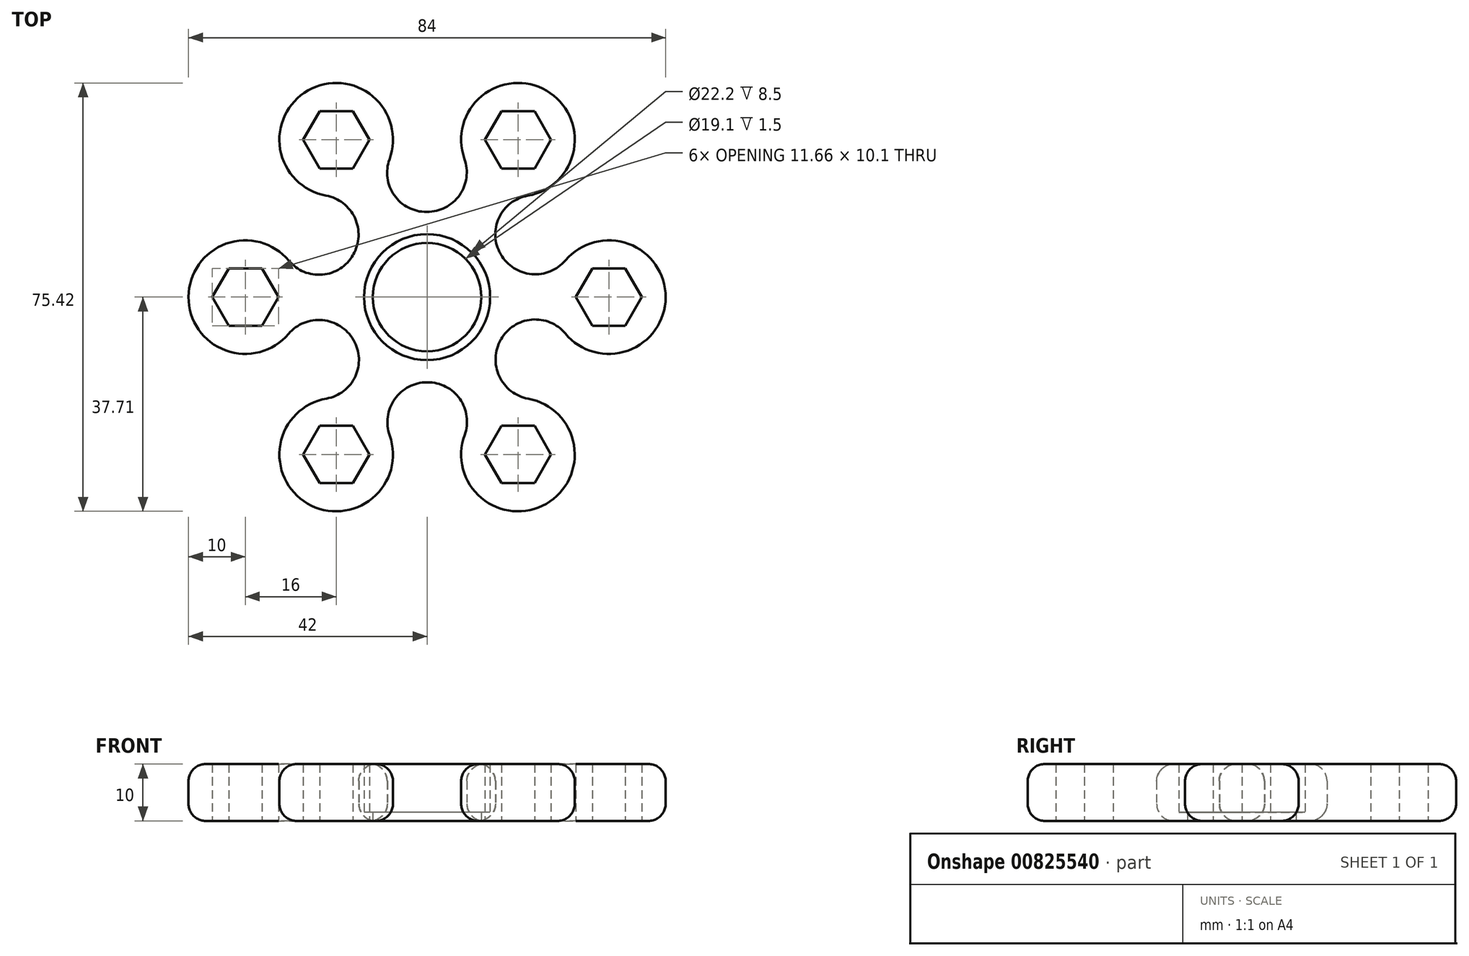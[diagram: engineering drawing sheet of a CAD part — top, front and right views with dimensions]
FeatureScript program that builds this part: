
annotation { "Feature Type Name" : "Feature", "Feature Type Description" : "" }
export const myFeature = defineFeature(function(context is Context, id is Id, definition is map)
    precondition{}
    {
        {
            var Q0;
            Q0=qCreatedBy(makeId("Top.planeOp"),FACE);
            var sketch = newSketch(context, id + "F0", { "sketchPlane" : qUnion([Q0])});
            skCircle(sketch, "E0", {"center": v(0, 0) * mm, "radius": 11.1 * mm});
            skLineSegment(sketch, "E1", {"start": v(0, 0) * mm, "end": v(32, 0) * mm});
            skCircle(sketch, "E2.cCircle", {"center": v(32, 0) * mm, "radius": 5.05 * mm, "construction": true});
            skLineSegment(sketch, "E2.0", {"start": v(34.92, -5.05) * mm, "end": v(29.08, -5.05) * mm});
            skLineSegment(sketch, "E2.1", {"start": v(29.08, -5.05) * mm, "end": v(26.17, 0) * mm});
            skLineSegment(sketch, "E2.2", {"start": v(26.17, 0) * mm, "end": v(29.08, 5.05) * mm});
            skLineSegment(sketch, "E2.3", {"start": v(29.08, 5.05) * mm, "end": v(34.92, 5.05) * mm});
            skLineSegment(sketch, "E2.4", {"start": v(34.92, 5.05) * mm, "end": v(37.83, 0) * mm});
            skLineSegment(sketch, "E2.5", {"start": v(37.83, 0) * mm, "end": v(34.92, -5.05) * mm});
            skPoint(sketch, "E2.0.midPoint", {"position": v(32, -5.05) * mm});
            skArc(sketch, "E3", {"start": v(12.99, 7.5) * mm, "mid": v(12.97, 7.54) * mm, "end": v(12.95, 7.58) * mm});
            skArc(sketch, "E4", {"start": v(24.33, -6.41) * mm, "mid": v(42, -0.04) * mm, "end": v(24.38, 6.48) * mm});
            skArc(sketch, "E5", {"start": v(12.99, 7.5) * mm, "mid": v(18.42, 4.04) * mm, "end": v(24.38, 6.48) * mm});
            skArc(sketch, "E6", {"start": v(24.33, -6.41) * mm, "mid": v(18.42, -3.96) * mm, "end": v(13.04, -7.42) * mm});
            skCircle(sketch, "E7.1.0", {"center": v(16, 27.71) * mm, "radius": 5.05 * mm, "construction": true});
            skArc(sketch, "E7.1.1", {"start": v(17.72, 17.86) * mm, "mid": v(21.04, 36.35) * mm, "end": v(6.58, 24.35) * mm});
            skPoint(sketch, "E7.1.2", {"position": v(20.37, 25.19) * mm});
            skLineSegment(sketch, "E7.1.3", {"start": v(13.08, 22.66) * mm, "end": v(10.17, 27.71) * mm});
            skArc(sketch, "E7.1.4", {"start": v(17.72, 17.86) * mm, "mid": v(12.64, 13.97) * mm, "end": v(12.95, 7.58) * mm});
            skArc(sketch, "E7.1.5", {"start": v(0, 15) * mm, "mid": v(5.71, 17.97) * mm, "end": v(6.58, 24.35) * mm});
            skLineSegment(sketch, "E7.1.6", {"start": v(21.83, 27.71) * mm, "end": v(18.92, 22.66) * mm});
            skLineSegment(sketch, "E7.1.7", {"start": v(18.92, 22.66) * mm, "end": v(13.08, 22.66) * mm});
            skLineSegment(sketch, "E7.1.8", {"start": v(13.08, 32.76) * mm, "end": v(18.92, 32.76) * mm});
            skLineSegment(sketch, "E7.1.9", {"start": v(10.17, 27.71) * mm, "end": v(13.08, 32.76) * mm});
            skLineSegment(sketch, "E7.1.10", {"start": v(18.92, 32.76) * mm, "end": v(21.83, 27.71) * mm});
            skCircle(sketch, "E7.2.0", {"center": v(-16, 27.71) * mm, "radius": 5.05 * mm, "construction": true});
            skArc(sketch, "E7.2.1", {"start": v(-6.61, 24.27) * mm, "mid": v(-20.96, 36.4) * mm, "end": v(-17.8, 17.88) * mm});
            skPoint(sketch, "E7.2.2", {"position": v(-11.63, 30.24) * mm});
            skLineSegment(sketch, "E7.2.3", {"start": v(-13.08, 22.66) * mm, "end": v(-18.92, 22.66) * mm});
            skArc(sketch, "E7.2.4", {"start": v(-6.61, 24.27) * mm, "mid": v(-5.78, 17.93) * mm, "end": v(-0.09, 15) * mm});
            skArc(sketch, "E7.2.5", {"start": v(-13, 7.5) * mm, "mid": v(-12.7, 13.93) * mm, "end": v(-17.8, 17.88) * mm});
            skLineSegment(sketch, "E7.2.6", {"start": v(-13.08, 32.76) * mm, "end": v(-10.17, 27.71) * mm});
            skLineSegment(sketch, "E7.2.7", {"start": v(-10.17, 27.71) * mm, "end": v(-13.08, 22.66) * mm});
            skLineSegment(sketch, "E7.2.8", {"start": v(-21.83, 27.71) * mm, "end": v(-18.92, 32.76) * mm});
            skLineSegment(sketch, "E7.2.9", {"start": v(-18.92, 22.66) * mm, "end": v(-21.83, 27.71) * mm});
            skLineSegment(sketch, "E7.2.10", {"start": v(-18.92, 32.76) * mm, "end": v(-13.08, 32.76) * mm});
            skCircle(sketch, "E7.3.0", {"center": v(-32, 0) * mm, "radius": 5.05 * mm, "construction": true});
            skArc(sketch, "E7.3.1", {"start": v(-24.33, 6.41) * mm, "mid": v(-42, 0.04) * mm, "end": v(-24.38, -6.48) * mm});
            skPoint(sketch, "E7.3.2", {"position": v(-32, 5.05) * mm});
            skLineSegment(sketch, "E7.3.3", {"start": v(-26.17, 0) * mm, "end": v(-29.08, -5.05) * mm});
            skArc(sketch, "E7.3.4", {"start": v(-24.33, 6.41) * mm, "mid": v(-18.42, 3.96) * mm, "end": v(-13.04, 7.42) * mm});
            skArc(sketch, "E7.3.5", {"start": v(-12.99, -7.5) * mm, "mid": v(-18.42, -4.04) * mm, "end": v(-24.38, -6.48) * mm});
            skLineSegment(sketch, "E7.3.6", {"start": v(-34.92, 5.05) * mm, "end": v(-29.08, 5.05) * mm});
            skLineSegment(sketch, "E7.3.7", {"start": v(-29.08, 5.05) * mm, "end": v(-26.17, 0) * mm});
            skLineSegment(sketch, "E7.3.8", {"start": v(-34.92, -5.05) * mm, "end": v(-37.83, 0) * mm});
            skLineSegment(sketch, "E7.3.9", {"start": v(-29.08, -5.05) * mm, "end": v(-34.92, -5.05) * mm});
            skLineSegment(sketch, "E7.3.10", {"start": v(-37.83, 0) * mm, "end": v(-34.92, 5.05) * mm});
            skCircle(sketch, "E7.4.0", {"center": v(-16, -27.71) * mm, "radius": 5.05 * mm, "construction": true});
            skArc(sketch, "E7.4.1", {"start": v(-17.72, -17.86) * mm, "mid": v(-21.04, -36.35) * mm, "end": v(-6.58, -24.35) * mm});
            skPoint(sketch, "E7.4.2", {"position": v(-20.37, -25.19) * mm});
            skLineSegment(sketch, "E7.4.3", {"start": v(-13.08, -22.66) * mm, "end": v(-10.17, -27.71) * mm});
            skArc(sketch, "E7.4.4", {"start": v(-17.72, -17.86) * mm, "mid": v(-12.64, -13.97) * mm, "end": v(-12.95, -7.58) * mm});
            skArc(sketch, "E7.4.5", {"start": v(0, -15) * mm, "mid": v(-5.71, -17.97) * mm, "end": v(-6.58, -24.35) * mm});
            skLineSegment(sketch, "E7.4.6", {"start": v(-21.83, -27.71) * mm, "end": v(-18.92, -22.66) * mm});
            skLineSegment(sketch, "E7.4.7", {"start": v(-18.92, -22.66) * mm, "end": v(-13.08, -22.66) * mm});
            skLineSegment(sketch, "E7.4.8", {"start": v(-13.08, -32.76) * mm, "end": v(-18.92, -32.76) * mm});
            skLineSegment(sketch, "E7.4.9", {"start": v(-10.17, -27.71) * mm, "end": v(-13.08, -32.76) * mm});
            skLineSegment(sketch, "E7.4.10", {"start": v(-18.92, -32.76) * mm, "end": v(-21.83, -27.71) * mm});
            skCircle(sketch, "E7.5.0", {"center": v(16, -27.71) * mm, "radius": 5.05 * mm, "construction": true});
            skArc(sketch, "E7.5.1", {"start": v(6.61, -24.27) * mm, "mid": v(20.96, -36.4) * mm, "end": v(17.8, -17.88) * mm});
            skPoint(sketch, "E7.5.2", {"position": v(11.63, -30.24) * mm});
            skLineSegment(sketch, "E7.5.3", {"start": v(13.08, -22.66) * mm, "end": v(18.92, -22.66) * mm});
            skArc(sketch, "E7.5.4", {"start": v(6.61, -24.27) * mm, "mid": v(5.78, -17.93) * mm, "end": v(0.09, -15) * mm});
            skArc(sketch, "E7.5.5", {"start": v(13, -7.5) * mm, "mid": v(12.7, -13.93) * mm, "end": v(17.8, -17.88) * mm});
            skLineSegment(sketch, "E7.5.6", {"start": v(13.08, -32.76) * mm, "end": v(10.17, -27.71) * mm});
            skLineSegment(sketch, "E7.5.7", {"start": v(10.17, -27.71) * mm, "end": v(13.08, -22.66) * mm});
            skLineSegment(sketch, "E7.5.8", {"start": v(21.83, -27.71) * mm, "end": v(18.92, -32.76) * mm});
            skLineSegment(sketch, "E7.5.9", {"start": v(18.92, -22.66) * mm, "end": v(21.83, -27.71) * mm});
            skLineSegment(sketch, "E7.5.10", {"start": v(18.92, -32.76) * mm, "end": v(13.08, -32.76) * mm});
            skArc(sketch, "E8.trimOffspring", {"start": v(0, 15) * mm, "mid": v(-0.05, 15) * mm, "end": v(-0.09, 15) * mm});
            skArc(sketch, "E9.trimOffspring", {"start": v(-13, 7.5) * mm, "mid": v(-13.01, 7.46) * mm, "end": v(-13.04, 7.42) * mm});
            skArc(sketch, "E10.trimOffspring", {"start": v(-12.99, -7.5) * mm, "mid": v(-12.97, -7.54) * mm, "end": v(-12.95, -7.58) * mm});
            skArc(sketch, "E11.trimOffspring", {"start": v(0, -15) * mm, "mid": v(0.05, -15) * mm, "end": v(0.09, -15) * mm});
            skArc(sketch, "E12.trimOffspring", {"start": v(13, -7.5) * mm, "mid": v(13.01, -7.46) * mm, "end": v(13.04, -7.42) * mm});
            skSolve(sketch);
        }
        {
            var Q0;
            Q0=makeQuery(id+"F0.imprint","IMPRINT",FACE,{"disambiguationData":[TD([[makeQuery(id+"F0.imprint","IMPRINT",EDGE,{"derivedFrom":sQuery(id+"F0.wireOp",EDGE,"E0")}),-1.0]])]});
            extrude(context, id + "F1", {"entities" : qUnion([Q0]), "depth" : 10 * mm, "offsetDistance" : 25 * mm});
        }
        {
            var Q0;
            Q0=qCreatedBy(makeId("Top.planeOp"),FACE);
            var sketch = newSketch(context, id + "F2", { "sketchPlane" : qUnion([Q0])});
            skCircle(sketch, "E13", {"center": v(0, 0) * mm, "radius": 11.1 * mm});
            skCircle(sketch, "E14", {"center": v(0, 0) * mm, "radius": 9.55 * mm});
            skSolve(sketch);
        }
        {
            var Q0;
            Q0 = qSketchRegion(id + "F2", true);
            extrude(context, id + "F3", {"entities" : qUnion([Q0]), "operationType" : NewBodyOperationType.ADD, "depth" : 1.5 * mm, "offsetDistance" : 25 * mm});
        }
        {
            var Q0;
            Q0=makeQuery(id+"F1.opExtrude","CAP_EDGE",EDGE,{"disambiguationData":[OSD([sQuery(id+"F0.wireOp",EDGE,"E7.5.1")])],"isStart":true});
            var Q1;
            Q1=makeQuery(id+"F1.opExtrude","CAP_EDGE",EDGE,{"disambiguationData":[OSD([sQuery(id+"F0.wireOp",EDGE,"E7.5.1")])],"isStart":false});
            fillet(context, id + "F4", {"entities" : qUnion([Q0, Q1]), "radius" : 3 * mm, "tangentPropagation" : true, "allowEdgeOverflow" : false});
        }
    });
